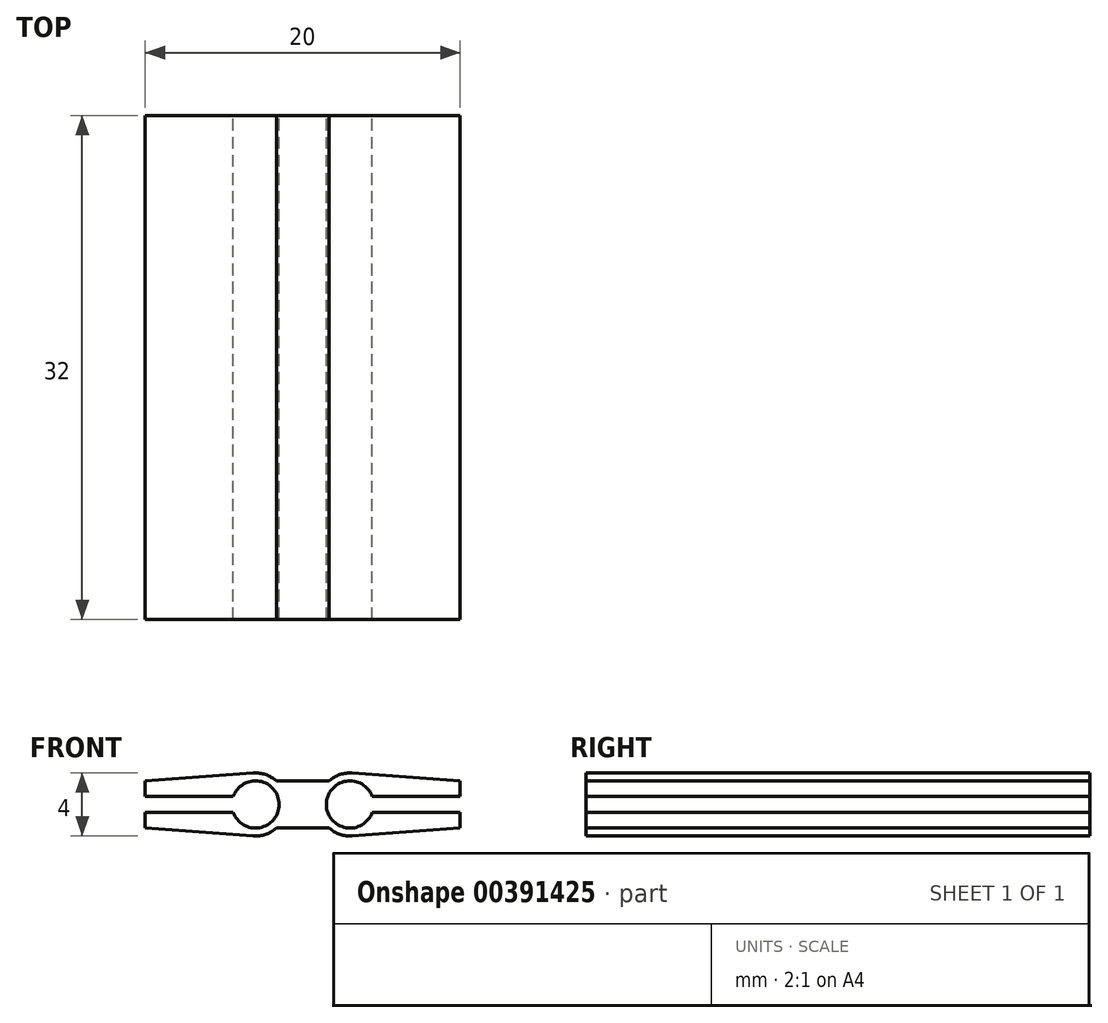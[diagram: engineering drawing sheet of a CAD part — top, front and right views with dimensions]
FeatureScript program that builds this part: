
annotation { "Feature Type Name" : "Feature", "Feature Type Description" : "" }
export const myFeature = defineFeature(function(context is Context, id is Id, definition is map)
    precondition{}
    {
        {
            var Q0;
            Q0=qCreatedBy(makeId("Front.planeOp"),FACE);
            var sketch = newSketch(context, id + "F0", { "sketchPlane" : qUnion([Q0])});
            skLineSegment(sketch, "E0.bottom", {"start": v(-6.66, 10.84) * mm, "end": v(13.34, 10.84) * mm});
            skLineSegment(sketch, "E0.top", {"start": v(-6.66, 7.84) * mm, "end": v(13.34, 7.84) * mm});
            skLineSegment(sketch, "E0.left", {"start": v(-6.66, 10.84) * mm, "end": v(-6.66, 7.84) * mm});
            skCircle(sketch, "E1", {"center": v(0.34, 9.34) * mm, "radius": 1.5 * mm});
            skLineSegment(sketch, "E2", {"start": v(-6.66, 9.34) * mm, "end": v(13.34, 9.34) * mm, "construction": true});
            skLineSegment(sketch, "E3", {"start": v(3.34, 10.84) * mm, "end": v(3.34, 7.84) * mm, "construction": true});
            skLineSegment(sketch, "E4", {"start": v(0.34, 9.34) * mm, "end": v(0.34, 9.84) * mm});
            skLineSegment(sketch, "E5", {"start": v(0.34, 9.84) * mm, "end": v(-6.8, 9.84) * mm});
            skLineSegment(sketch, "E6", {"start": v(-6.8, 9.84) * mm, "end": v(-6.8, 8.84) * mm});
            skLineSegment(sketch, "E7", {"start": v(-6.8, 8.84) * mm, "end": v(0.34, 8.84) * mm});
            skLineSegment(sketch, "E8", {"start": v(0.34, 8.84) * mm, "end": v(0.34, 9.34) * mm});
            skCircle(sketch, "E9.0", {"center": v(0.34, 9.34) * mm, "radius": 2 * mm});
            skLineSegment(sketch, "E10", {"start": v(-6.66, 10.84) * mm, "end": v(0.2, 11.33) * mm});
            skLineSegment(sketch, "E11", {"start": v(-6.66, 7.84) * mm, "end": v(0.2, 7.34) * mm});
            skLineSegment(sketch, "E12.MirrorCS", {"start": v(6.34, 9.34) * mm, "end": v(6.34, 9.84) * mm});
            skLineSegment(sketch, "E13.MirrorCS", {"start": v(6.34, 8.84) * mm, "end": v(6.34, 9.34) * mm});
            skLineSegment(sketch, "E14.MirrorCS", {"start": v(13.48, 9.84) * mm, "end": v(13.48, 8.84) * mm});
            skCircle(sketch, "E15.MirrorC", {"center": v(6.34, 9.34) * mm, "radius": 1.5 * mm});
            skLineSegment(sketch, "E16.MirrorCS", {"start": v(6.34, 9.84) * mm, "end": v(13.48, 9.84) * mm});
            skLineSegment(sketch, "E17.MirrorCS", {"start": v(13.34, 10.84) * mm, "end": v(6.49, 11.33) * mm});
            skLineSegment(sketch, "E18.MirrorCS", {"start": v(13.34, 7.84) * mm, "end": v(6.49, 7.34) * mm});
            skLineSegment(sketch, "E19.MirrorCS", {"start": v(13.48, 8.84) * mm, "end": v(6.34, 8.84) * mm});
            skCircle(sketch, "E20.MirrorC", {"center": v(6.34, 9.34) * mm, "radius": 2 * mm});
            skLineSegment(sketch, "E21.MirrorCS", {"start": v(13.34, 10.84) * mm, "end": v(13.34, 7.84) * mm});
            skSolve(sketch);
        }
        {
            var Q0;
            {var subQ0=sQuery(id+"F0.wireOp",EDGE,"08b192b2-85ac-4e08-a141-6e1c525e120e4.MirrorCS");var subQ1=sQuery(id+"F0.wireOp",EDGE,"E0.bottom");var subQ2=makeQuery(id+"F0.imprint","INTERSECT",VERTEX,{"derivedFrom":[subQ1,subQ0]});Q0=makeQuery(id+"F0.imprint","IMPRINT",FACE,{"disambiguationData":[TD([[makeQuery(id+"F0.imprint","IMPRINT",EDGE,{"disambiguationData":[TD([[subQ2,1.0]])],"derivedFrom":subQ1}),-1.0]])]});}
            var Q1;
            {var subQ3=sQuery(id+"F0.wireOp",EDGE,"E9.0");var subQ10=sQuery(id+"F0.wireOp",EDGE,"E0.bottom");var subQ11=makeQuery(id+"F0.imprint","INTERSECT",VERTEX,{"disambiguationData":[OD(0.0)],"derivedFrom":[subQ10,subQ3]});Q1=makeQuery(id+"F0.imprint","IMPRINT",FACE,{"disambiguationData":[TD([[makeQuery(id+"F0.imprint","IMPRINT",EDGE,{"disambiguationData":[TD([[subQ11,-1.0]])],"derivedFrom":subQ10}),-1.0]])]});}
            var Q2;
            {var subQ0=sQuery(id+"F0.wireOp",EDGE,"E9.0");var subQ1=sQuery(id+"F0.wireOp",EDGE,"E0.bottom");var subQ2=makeQuery(id+"F0.imprint","INTERSECT",VERTEX,{"disambiguationData":[OD(0.0)],"derivedFrom":[subQ1,subQ0]});Q2=makeQuery(id+"F0.imprint","IMPRINT",FACE,{"disambiguationData":[TD([[makeQuery(id+"F0.imprint","IMPRINT",EDGE,{"disambiguationData":[TD([[subQ2,-1.0]])],"derivedFrom":subQ1}),1.0]])]});}
            var Q3;
            {var subQ0=sQuery(id+"F0.wireOp",EDGE,"E9.0");var subQ1=sQuery(id+"F0.wireOp",EDGE,"E0.top");var subQ2=makeQuery(id+"F0.imprint","INTERSECT",VERTEX,{"disambiguationData":[OD(0.0)],"derivedFrom":[subQ1,subQ0]});Q3=makeQuery(id+"F0.imprint","IMPRINT",FACE,{"disambiguationData":[TD([[makeQuery(id+"F0.imprint","IMPRINT",EDGE,{"disambiguationData":[TD([[subQ2,-1.0]])],"derivedFrom":subQ1}),-1.0]])]});}
            var Q4;
            {var subQ0=sQuery(id+"F0.wireOp",EDGE,"E9.0");var subQ1=sQuery(id+"F0.wireOp",EDGE,"E0.bottom");var subQ2=makeQuery(id+"F0.imprint","INTERSECT",VERTEX,{"disambiguationData":[OD(1.0)],"derivedFrom":[subQ1,subQ0]});Q4=makeQuery(id+"F0.imprint","IMPRINT",FACE,{"disambiguationData":[TD([[makeQuery(id+"F0.imprint","IMPRINT",EDGE,{"disambiguationData":[TD([[subQ2,1.0]])],"derivedFrom":subQ1}),-1.0]])]});}
            var Q5;
            {var subQ0=sQuery(id+"F0.wireOp",EDGE,"E9.0");var subQ1=sQuery(id+"F0.wireOp",EDGE,"E0.bottom");var subQ2=makeQuery(id+"F0.imprint","INTERSECT",VERTEX,{"disambiguationData":[OD(1.0)],"derivedFrom":[subQ1,subQ0]});Q5=makeQuery(id+"F0.imprint","IMPRINT",FACE,{"disambiguationData":[TD([[makeQuery(id+"F0.imprint","IMPRINT",EDGE,{"disambiguationData":[TD([[subQ2,-1.0]])],"derivedFrom":subQ1}),-1.0]])]});}
            var Q6;
            {var subQ0=sQuery(id+"F0.wireOp",EDGE,"E9.0");var subQ1=sQuery(id+"F0.wireOp",EDGE,"E0.top");var subQ2=makeQuery(id+"F0.imprint","INTERSECT",VERTEX,{"disambiguationData":[OD(0.0)],"derivedFrom":[subQ1,subQ0]});Q6=makeQuery(id+"F0.imprint","IMPRINT",FACE,{"disambiguationData":[TD([[makeQuery(id+"F0.imprint","IMPRINT",EDGE,{"disambiguationData":[TD([[subQ2,-1.0]])],"derivedFrom":subQ1}),1.0]])]});}
            var Q7;
            {var subQ0=sQuery(id+"F0.wireOp",EDGE,"E0.left");var subQ1=sQuery(id+"F0.wireOp",EDGE,"E0.top");var subQ2=makeQuery(id+"F0.imprint","INTERSECT",VERTEX,{"derivedFrom":[subQ1,subQ0]});Q7=makeQuery(id+"F0.imprint","IMPRINT",FACE,{"disambiguationData":[TD([[makeQuery(id+"F0.imprint","IMPRINT",EDGE,{"disambiguationData":[TD([[subQ2,-1.0]])],"derivedFrom":subQ1}),1.0]])]});}
            var Q8;
            {var subQ0=sQuery(id+"F0.wireOp",EDGE,"E0.left");var subQ1=sQuery(id+"F0.wireOp",EDGE,"E0.bottom");var subQ2=makeQuery(id+"F0.imprint","INTERSECT",VERTEX,{"derivedFrom":[subQ1,subQ0]});Q8=makeQuery(id+"F0.imprint","IMPRINT",FACE,{"disambiguationData":[TD([[makeQuery(id+"F0.imprint","IMPRINT",EDGE,{"disambiguationData":[TD([[subQ2,-1.0]])],"derivedFrom":subQ1}),-1.0]])]});}
            var Q9;
            {var subQ0=sQuery(id+"F0.wireOp",EDGE,"b6edabe3-c984-4cd1-b3f5-f1b69bc57e210.MirrorC");var subQ1=sQuery(id+"F0.wireOp",EDGE,"E0.bottom");var subQ2=makeQuery(id+"F0.imprint","INTERSECT",VERTEX,{"disambiguationData":[OD(0.0)],"derivedFrom":[subQ1,subQ0]});Q9=makeQuery(id+"F0.imprint","IMPRINT",FACE,{"disambiguationData":[TD([[makeQuery(id+"F0.imprint","IMPRINT",EDGE,{"disambiguationData":[TD([[subQ2,-1.0]])],"derivedFrom":subQ1}),-1.0]])]});}
            var Q10;
            {var subQ0=sQuery(id+"F0.wireOp",EDGE,"b6edabe3-c984-4cd1-b3f5-f1b69bc57e210.MirrorC");var subQ1=sQuery(id+"F0.wireOp",EDGE,"E0.bottom");var subQ2=makeQuery(id+"F0.imprint","INTERSECT",VERTEX,{"disambiguationData":[OD(0.0)],"derivedFrom":[subQ1,subQ0]});Q10=makeQuery(id+"F0.imprint","IMPRINT",FACE,{"disambiguationData":[TD([[makeQuery(id+"F0.imprint","IMPRINT",EDGE,{"disambiguationData":[TD([[subQ2,-1.0]])],"derivedFrom":subQ1}),1.0]])]});}
            var Q11;
            {var subQ0=sQuery(id+"F0.wireOp",EDGE,"b6edabe3-c984-4cd1-b3f5-f1b69bc57e210.MirrorC");var subQ1=sQuery(id+"F0.wireOp",EDGE,"E0.bottom");var subQ2=makeQuery(id+"F0.imprint","INTERSECT",VERTEX,{"disambiguationData":[OD(1.0)],"derivedFrom":[subQ1,subQ0]});Q11=makeQuery(id+"F0.imprint","IMPRINT",FACE,{"disambiguationData":[TD([[makeQuery(id+"F0.imprint","IMPRINT",EDGE,{"disambiguationData":[TD([[subQ2,1.0]])],"derivedFrom":subQ1}),-1.0]])]});}
            var Q12;
            {var subQ0=sQuery(id+"F0.wireOp",EDGE,"b6edabe3-c984-4cd1-b3f5-f1b69bc57e210.MirrorC");var subQ1=sQuery(id+"F0.wireOp",EDGE,"E0.top");var subQ2=makeQuery(id+"F0.imprint","INTERSECT",VERTEX,{"disambiguationData":[OD(1.0)],"derivedFrom":[subQ1,subQ0]});Q12=makeQuery(id+"F0.imprint","IMPRINT",FACE,{"disambiguationData":[TD([[makeQuery(id+"F0.imprint","IMPRINT",EDGE,{"disambiguationData":[TD([[subQ2,1.0]])],"derivedFrom":subQ1}),1.0]])]});}
            var Q13;
            {var subQ0=sQuery(id+"F0.wireOp",EDGE,"08b192b2-85ac-4e08-a141-6e1c525e120e4.MirrorCS");var subQ1=sQuery(id+"F0.wireOp",EDGE,"E0.top");var subQ2=makeQuery(id+"F0.imprint","INTERSECT",VERTEX,{"derivedFrom":[subQ1,subQ0]});Q13=makeQuery(id+"F0.imprint","IMPRINT",FACE,{"disambiguationData":[TD([[makeQuery(id+"F0.imprint","IMPRINT",EDGE,{"disambiguationData":[TD([[subQ2,1.0]])],"derivedFrom":subQ1}),1.0]])]});}
            var Q14;
            {var subQ0=sQuery(id+"F0.wireOp",EDGE,"b6edabe3-c984-4cd1-b3f5-f1b69bc57e210.MirrorC");var subQ1=sQuery(id+"F0.wireOp",EDGE,"E0.top");var subQ2=makeQuery(id+"F0.imprint","INTERSECT",VERTEX,{"disambiguationData":[OD(0.0)],"derivedFrom":[subQ1,subQ0]});Q14=makeQuery(id+"F0.imprint","IMPRINT",FACE,{"disambiguationData":[TD([[makeQuery(id+"F0.imprint","IMPRINT",EDGE,{"disambiguationData":[TD([[subQ2,-1.0]])],"derivedFrom":subQ1}),-1.0]])]});}
            var Q15;
            {var subQ0=sQuery(id+"F0.wireOp",EDGE,"E10");Q15=makeQuery(id+"F0.imprint","IMPRINT",FACE,{"disambiguationData":[TD([[makeQuery(id+"F0.imprint","IMPRINT",EDGE,{"derivedFrom":subQ0}),-1.0]])]});}
            var Q16;
            {var subQ0=sQuery(id+"F0.wireOp",EDGE,"E11");Q16=makeQuery(id+"F0.imprint","IMPRINT",FACE,{"disambiguationData":[TD([[makeQuery(id+"F0.imprint","IMPRINT",EDGE,{"derivedFrom":subQ0}),1.0]])]});}
            var Q17;
            {var subQ0=sQuery(id+"F0.wireOp",EDGE,"E9.0");var subQ1=sQuery(id+"F0.wireOp",EDGE,"E0.bottom");var subQ2=makeQuery(id+"F0.imprint","INTERSECT",VERTEX,{"disambiguationData":[OD(1.0)],"derivedFrom":[subQ1,subQ0]});Q17=makeQuery(id+"F0.imprint","IMPRINT",FACE,{"disambiguationData":[TD([[makeQuery(id+"F0.imprint","IMPRINT",EDGE,{"disambiguationData":[TD([[subQ2,-1.0]])],"derivedFrom":subQ1}),1.0]])]});}
            var Q18;
            {var subQ0=sQuery(id+"F0.wireOp",EDGE,"E9.0");var subQ1=sQuery(id+"F0.wireOp",EDGE,"E0.top");var subQ2=makeQuery(id+"F0.imprint","INTERSECT",VERTEX,{"disambiguationData":[OD(1.0)],"derivedFrom":[subQ1,subQ0]});Q18=makeQuery(id+"F0.imprint","IMPRINT",FACE,{"disambiguationData":[TD([[makeQuery(id+"F0.imprint","IMPRINT",EDGE,{"disambiguationData":[TD([[subQ2,-1.0]])],"derivedFrom":subQ1}),-1.0]])]});}
            var Q19;
            {var subQ0=sQuery(id+"F0.wireOp",EDGE,"E21.MirrorCS");var subQ5=sQuery(id+"F0.wireOp",EDGE,"E16.MirrorCS");var subQ6=makeQuery(id+"F0.imprint","INTERSECT",VERTEX,{"derivedFrom":[subQ5,subQ0]});Q19=makeQuery(id+"F0.imprint","IMPRINT",FACE,{"disambiguationData":[TD([[makeQuery(id+"F0.imprint","IMPRINT",EDGE,{"disambiguationData":[TD([[subQ6,1.0]])],"derivedFrom":subQ5}),1.0]])]});}
            var Q20;
            {var subQ0=sQuery(id+"F0.wireOp",EDGE,"E21.MirrorCS");var subQ5=sQuery(id+"F0.wireOp",EDGE,"E19.MirrorCS");var subQ7=makeQuery(id+"F0.imprint","INTERSECT",VERTEX,{"derivedFrom":[subQ5,subQ0]});Q20=makeQuery(id+"F0.imprint","IMPRINT",FACE,{"disambiguationData":[TD([[makeQuery(id+"F0.imprint","IMPRINT",EDGE,{"disambiguationData":[TD([[subQ7,-1.0]])],"derivedFrom":subQ5}),1.0]])]});}
            var Q21;
            {var subQ0=sQuery(id+"F0.wireOp",EDGE,"E18.MirrorCS");Q21=makeQuery(id+"F0.imprint","IMPRINT",FACE,{"disambiguationData":[TD([[makeQuery(id+"F0.imprint","IMPRINT",EDGE,{"derivedFrom":subQ0}),-1.0]])]});}
            var Q22;
            {var subQ0=sQuery(id+"F0.wireOp",EDGE,"E20.MirrorC");var subQ1=sQuery(id+"F0.wireOp",EDGE,"E0.top");var subQ2=makeQuery(id+"F0.imprint","INTERSECT",VERTEX,{"disambiguationData":[OD(0.0)],"derivedFrom":[subQ1,subQ0]});Q22=makeQuery(id+"F0.imprint","IMPRINT",FACE,{"disambiguationData":[TD([[makeQuery(id+"F0.imprint","IMPRINT",EDGE,{"disambiguationData":[TD([[subQ2,-1.0]])],"derivedFrom":subQ1}),-1.0]])]});}
            var Q23;
            {var subQ0=sQuery(id+"F0.wireOp",EDGE,"E20.MirrorC");var subQ1=sQuery(id+"F0.wireOp",EDGE,"E0.bottom");var subQ2=makeQuery(id+"F0.imprint","INTERSECT",VERTEX,{"disambiguationData":[OD(0.0)],"derivedFrom":[subQ1,subQ0]});Q23=makeQuery(id+"F0.imprint","IMPRINT",FACE,{"disambiguationData":[TD([[makeQuery(id+"F0.imprint","IMPRINT",EDGE,{"disambiguationData":[TD([[subQ2,-1.0]])],"derivedFrom":subQ1}),1.0]])]});}
            var Q24;
            {var subQ0=sQuery(id+"F0.wireOp",EDGE,"E17.MirrorCS");Q24=makeQuery(id+"F0.imprint","IMPRINT",FACE,{"disambiguationData":[TD([[makeQuery(id+"F0.imprint","IMPRINT",EDGE,{"derivedFrom":subQ0}),1.0]])]});}
            extrude(context, id + "F1", {"entities" : qUnion([Q0, Q1, Q2, Q3, Q4, Q5, Q6, Q7, Q8, Q9, Q10, Q11, Q12, Q13, Q14, Q15, Q16, Q17, Q18, Q19, Q20, Q21, Q22, Q23, Q24]), "depth" : 32 * mm});
        }
    });
